# Revit family: Shower-Controller_Mounting_Bracket-KOHLER-DTV-K-99694
name_source: partatom
category: Specialty Equipment
revit_build: Autodesk Revit 2015 (Build: 20140606_1530(x64)
units: mm (PartAtom-declared; Revit-internal decimal feet)

## types (5) — shared parameters
ADA Compliant = No
Assembly Code = C1030200
Date Modified = 11/14/2018
Default Elevation = 58"
Description = Interface mounting bracket
Height = 5 5/8"
Length = 1"
Manufacturer = KOHLER Co.
MasterFormat 1995 = 10820
MasterFormat 2004 = 10.28.13
Material = Metal Construction
Product Documentation Link = http://www.us.kohler.com
Product Name = DTV+
Product Page URL = http://www.us.kohler.com
URL = https://www.us.kohler.com
Width = 3 5/16"

## per-type parameters (varying)
| type | Finish | Model | Type |
| CP-Polished Chrome | Kohler-Metal-CP-Polished_Chrome | K-99694-CP | 1 |
| SN-Vibrant Polished Nickel | Kohler-Metal-SN-Vibrant_Polished_Nickel | K-99694-SN | 2 |
| BN-Vibrant Brushed Nickel | Kohler-Metal-BN-Vibrant_Brushed_Nickel | K-99694-BN | 3 |
| BL-Matte Black | Kohler-Metal-BL-Matte_Black | K-99694-BL | 4 |
| TT-Titanium | Kohler-Metal-TT-Vibrant_Titanium | K-99694-TT | 5 |

## geometry (parser evidence)
native form markers: Sweep x4
no freeform markers — native parametric forms only
